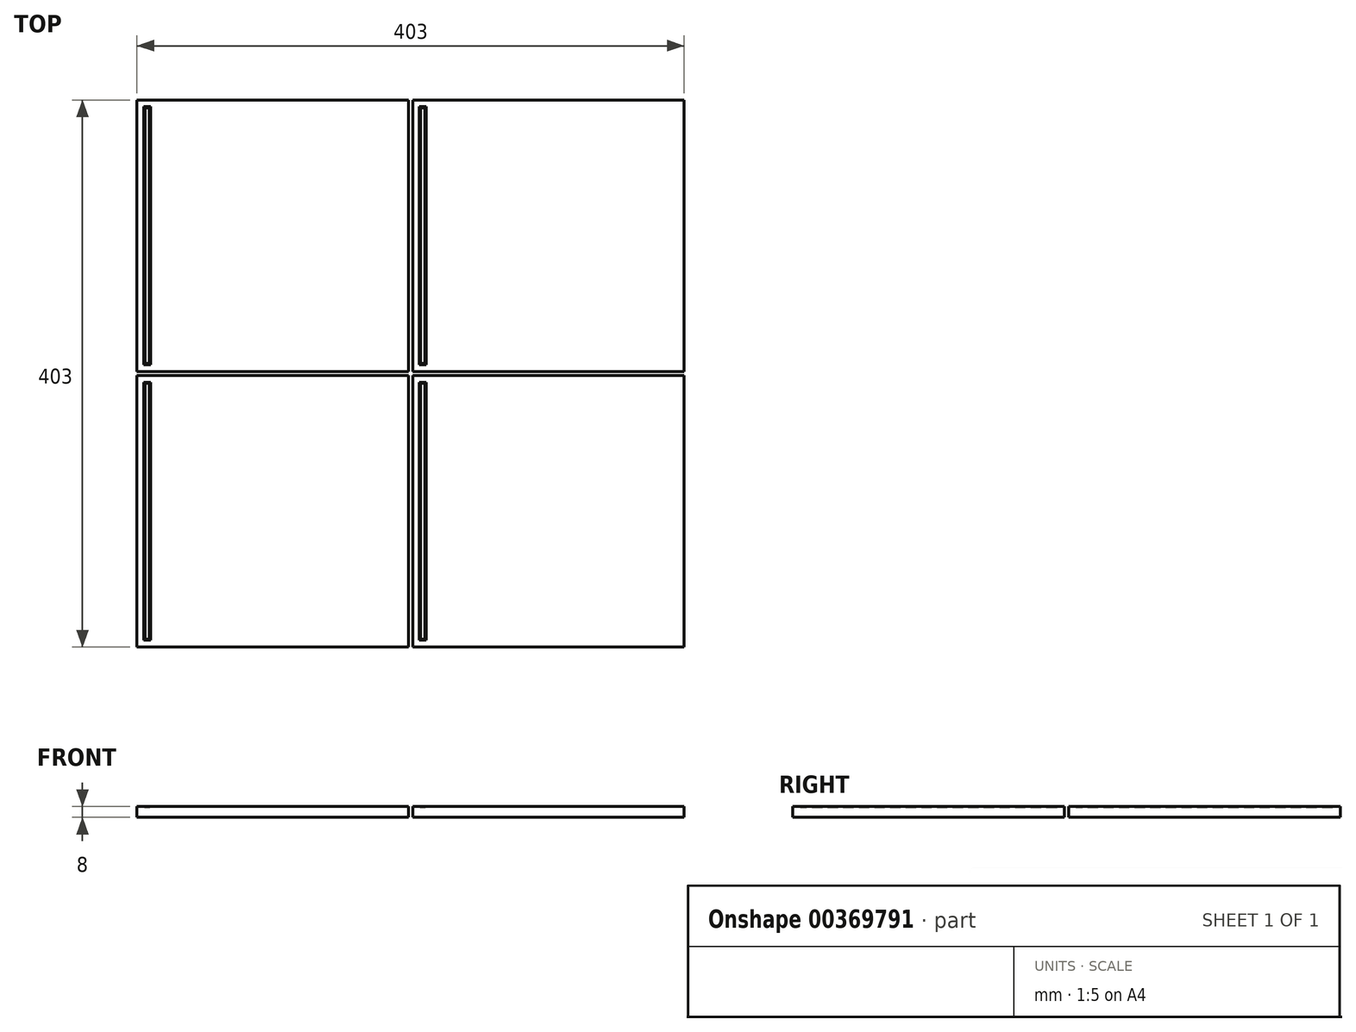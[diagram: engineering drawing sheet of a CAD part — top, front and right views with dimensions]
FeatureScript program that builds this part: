
annotation { "Feature Type Name" : "Feature", "Feature Type Description" : "" }
export const myFeature = defineFeature(function(context is Context, id is Id, definition is map)
    precondition{}
    {
        {
            var Q0;
            Q0=qCreatedBy(makeId("Top.planeOp"),FACE);
            var sketch = newSketch(context, id + "F0", { "sketchPlane" : qUnion([Q0])});
            skLineSegment(sketch, "E0.bottom", {"start": v(100, -100) * mm, "end": v(-100, -100) * mm});
            skLineSegment(sketch, "E0.top", {"start": v(100, 100) * mm, "end": v(-100, 100) * mm});
            skLineSegment(sketch, "E0.left", {"start": v(100, -100) * mm, "end": v(100, 100) * mm});
            skLineSegment(sketch, "E0.right", {"start": v(-100, -100) * mm, "end": v(-100, 100) * mm});
            skPoint(sketch, "E0.middle", {"position": v(0, 0) * mm});
            skLineSegment(sketch, "E1.bottom", {"start": v(-95, 95) * mm, "end": v(-90, 95) * mm});
            skLineSegment(sketch, "E1.top", {"start": v(-95, -95) * mm, "end": v(-90, -95) * mm});
            skLineSegment(sketch, "E1.left", {"start": v(-95, 95) * mm, "end": v(-95, -95) * mm});
            skLineSegment(sketch, "E1.right", {"start": v(-90, 95) * mm, "end": v(-90, -95) * mm});
            skSolve(sketch);
        }
        {
            var Q0;
            Q0=makeQuery(id+"F0.imprint","IMPRINT",FACE,{"disambiguationData":[TD([[makeQuery(id+"F0.imprint","IMPRINT",EDGE,{"derivedFrom":sQuery(id+"F0.wireOp",EDGE,"E0.bottom")}),-1.0]])]});
            var Q1;
            Q1=makeQuery(id+"F0.imprint","IMPRINT",FACE,{"disambiguationData":[TD([[makeQuery(id+"F0.imprint","IMPRINT",EDGE,{"derivedFrom":sQuery(id+"F0.wireOp",EDGE,"E1.bottom")}),-1.0]])]});
            extrude(context, id + "F1", {"entities" : qUnion([Q0, Q1]), "depth" : 8 * mm});
        }
        {
            var Q0;
            Q0=makeQuery(id+"F1.opExtrude","CAP_FACE",FACE,{"disambiguationData":[OSD([sQuery(id+"F0.wireOp",EDGE,"E0.bottom"),sQuery(id+"F0.wireOp",EDGE,"E0.top"),sQuery(id+"F0.wireOp",EDGE,"E0.left"),sQuery(id+"F0.wireOp",EDGE,"E0.right")])],"isStart":false});
            var sketch = newSketch(context, id + "F2", { "sketchPlane" : qUnion([Q0])});
            skLineSegment(sketch, "E2.0", {"start": v(-90, 95) * mm, "end": v(-90, -95) * mm});
            skLineSegment(sketch, "E2.1", {"start": v(-95, 95) * mm, "end": v(-95, -95) * mm});
            skPoint(sketch, "E2.2", {"position": v(-92.5, 95) * mm});
            skPoint(sketch, "E2.3", {"position": v(-92.5, -95) * mm});
            skLineSegment(sketch, "E3.0", {"start": v(-95, 95) * mm, "end": v(-90, 95) * mm});
            skLineSegment(sketch, "E4.0", {"start": v(-95, -95) * mm, "end": v(-90, -95) * mm});
            skSolve(sketch);
        }
        {
            var Q0;
            Q0=makeQuery(id+"F2.imprint","IMPRINT",FACE,{"disambiguationData":[TD([[makeQuery(id+"F2.imprint","IMPRINT",EDGE,{"derivedFrom":sQuery(id+"F2.wireOp",EDGE,"E2.0")}),-1.0]])]});
            extrude(context, id + "F3", {"entities" : qUnion([Q0]), "operationType" : NewBodyOperationType.REMOVE, "oppositeDirection" : true, "depth" : 1 * mm, "hasDraft" : true, "draftAngle" : 40 * degree, "draftPullDirection" : true});
        }
        {
            var Q0;
            Q0=makeQuery(id+"F1.opExtrude","SWEPT_BODY",BODY,{"disambiguationData":[OSD([sQuery(id+"F0.wireOp",EDGE,"E0.bottom"),sQuery(id+"F0.wireOp",EDGE,"E0.top"),sQuery(id+"F0.wireOp",EDGE,"E0.left"),sQuery(id+"F0.wireOp",EDGE,"E0.right")])]});
            transform(context, id + "F4", {"entities" : qUnion([Q0]), "transformType" : TransformType.TRANSLATION_3D, "dx" : 0 * mm, "dy" : 203 * mm, "dz" : 0 * mm, "makeCopy" : true});
        }
        {
            var Q0;
            Q0=makeQuery(id+"F1.opExtrude","SWEPT_BODY",BODY,{"disambiguationData":[OSD([sQuery(id+"F0.wireOp",EDGE,"E0.bottom"),sQuery(id+"F0.wireOp",EDGE,"E0.top"),sQuery(id+"F0.wireOp",EDGE,"E0.left"),sQuery(id+"F0.wireOp",EDGE,"E0.right")])]});
            transform(context, id + "F5", {"entities" : qUnion([Q0]), "transformType" : TransformType.TRANSLATION_3D, "dx" : 203 * mm, "dy" : 0 * mm, "dz" : 0 * mm, "makeCopy" : true});
        }
        {
            var Q0;
            Q0=makeQuery(id+"F4.opPattern","COPY",BODY,{"derivedFrom":makeQuery(id+"F1.opExtrude","SWEPT_BODY",BODY,{"disambiguationData":[OSD([sQuery(id+"F0.wireOp",EDGE,"E0.bottom"),sQuery(id+"F0.wireOp",EDGE,"E0.top"),sQuery(id+"F0.wireOp",EDGE,"E0.left"),sQuery(id+"F0.wireOp",EDGE,"E0.right")])]}),"instanceName":"1"});
            transform(context, id + "F6", {"entities" : qUnion([Q0]), "transformType" : TransformType.TRANSLATION_3D, "dx" : 203 * mm, "dy" : 0 * mm, "dz" : 0 * mm, "makeCopy" : true});
        }
    });
